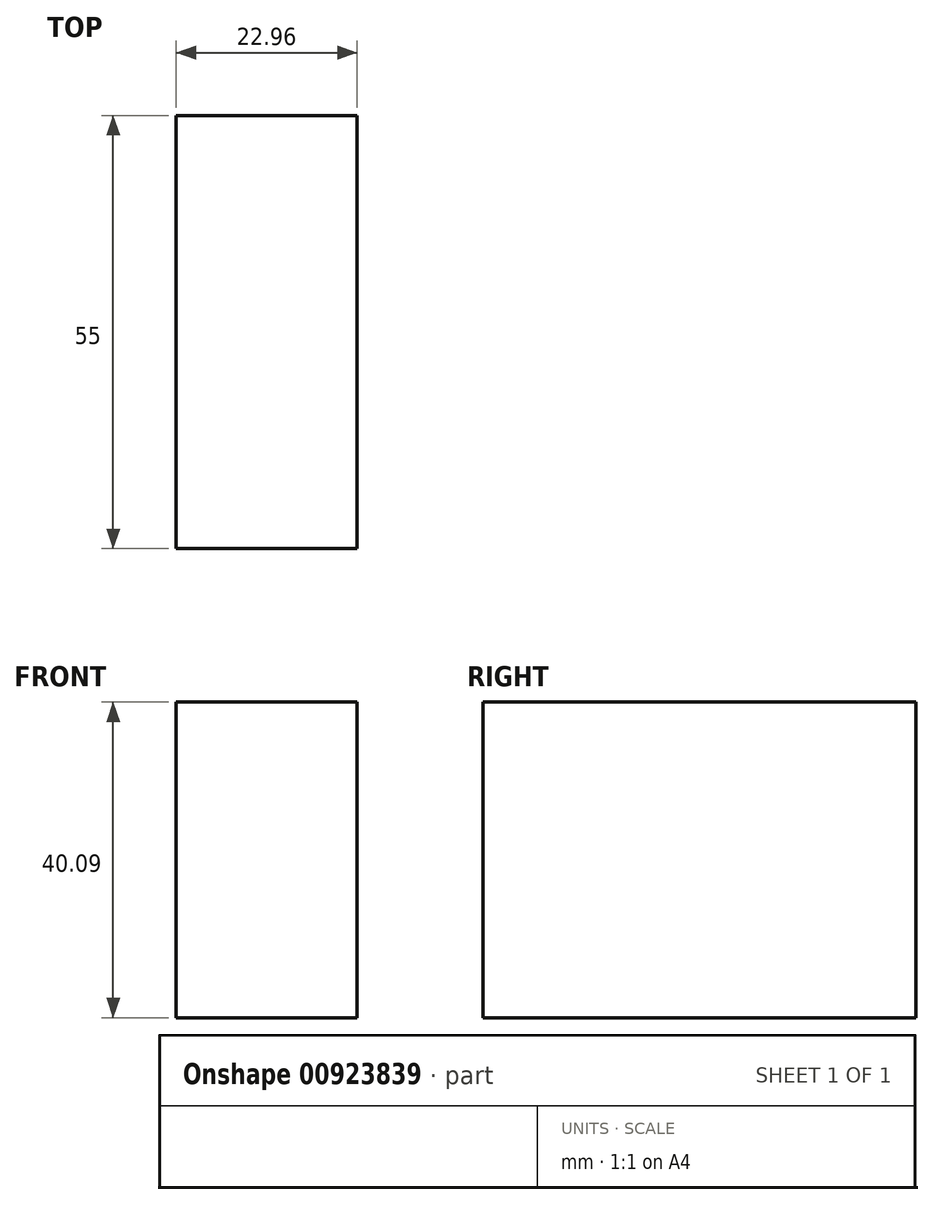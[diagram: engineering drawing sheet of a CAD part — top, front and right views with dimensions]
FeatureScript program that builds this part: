
annotation { "Feature Type Name" : "Feature", "Feature Type Description" : "" }
export const myFeature = defineFeature(function(context is Context, id is Id, definition is map)
    precondition{}
    {
        {
            var Q0;
            Q0=qCreatedBy(makeId("Front.planeOp"),FACE);
            var sketch = newSketch(context, id + "F0", { "sketchPlane" : qUnion([Q0])});
            skLineSegment(sketch, "E0.bottom", {"start": v(46.78, 0) * mm, "end": v(69.74, 0) * mm});
            skLineSegment(sketch, "E0.top", {"start": v(46.78, 40.09) * mm, "end": v(69.74, 40.09) * mm});
            skLineSegment(sketch, "E0.left", {"start": v(46.78, 0) * mm, "end": v(46.78, 40.09) * mm});
            skLineSegment(sketch, "E0.right", {"start": v(69.74, 0) * mm, "end": v(69.74, 40.09) * mm});
            skSolve(sketch);
        }
        {
            var Q0;
            Q0 = qSketchRegion(id + "F0", true);
            extrude(context, id + "F1", {"entities" : qUnion([Q0]), "depth" : 55 * mm, "offsetDistance" : 25 * mm});
        }
    });
